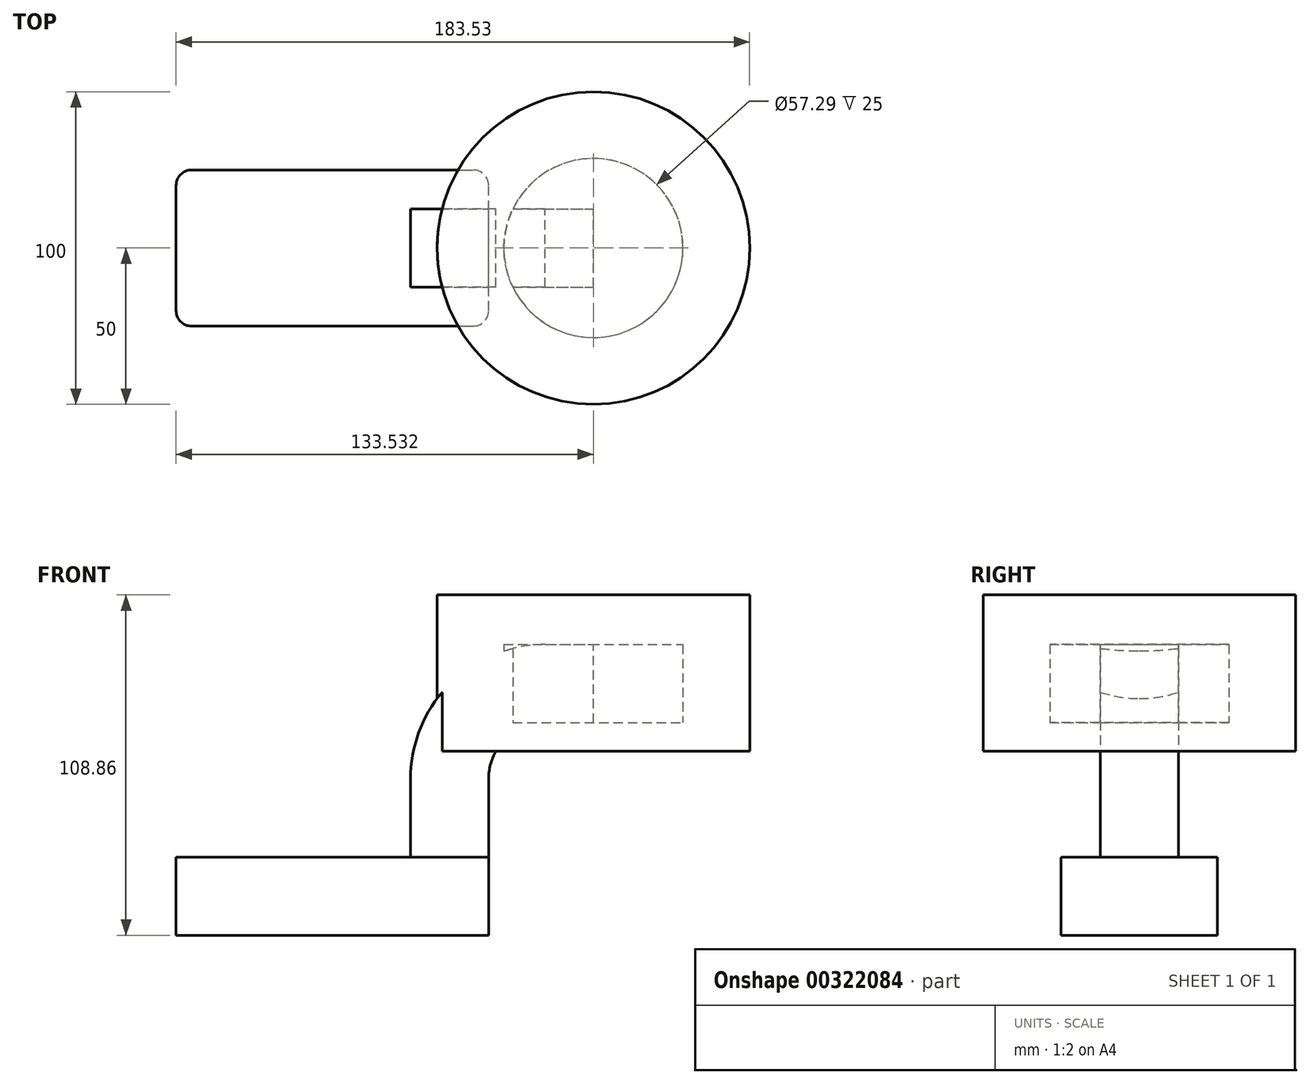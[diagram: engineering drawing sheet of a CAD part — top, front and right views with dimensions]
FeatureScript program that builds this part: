
annotation { "Feature Type Name" : "Feature", "Feature Type Description" : "" }
export const myFeature = defineFeature(function(context is Context, id is Id, definition is map)
    precondition{}
    {
        {
            var Q0;
            Q0=qCreatedBy(makeId("Front.planeOp"),FACE);
            var sketch = newSketch(context, id + "F0", { "sketchPlane" : qUnion([Q0])});
            skLineSegment(sketch, "E0.bottom", {"start": v(-50, 12.5) * mm, "end": v(50, 12.5) * mm});
            skLineSegment(sketch, "E0.top", {"start": v(-50, -12.5) * mm, "end": v(50, -12.5) * mm});
            skLineSegment(sketch, "E0.left", {"start": v(-50, 12.5) * mm, "end": v(-50, -12.5) * mm});
            skLineSegment(sketch, "E0.right", {"start": v(50, 12.5) * mm, "end": v(50, -12.5) * mm});
            skPoint(sketch, "E0.middle", {"position": v(0, 0) * mm});
            skLineSegment(sketch, "E1.bottom", {"start": v(133.53, 46.36) * mm, "end": v(83.53, 46.36) * mm});
            skLineSegment(sketch, "E1.top", {"start": v(133.53, 96.36) * mm, "end": v(83.53, 96.36) * mm});
            skLineSegment(sketch, "E1.left", {"start": v(133.53, 46.36) * mm, "end": v(133.53, 96.36) * mm});
            skLineSegment(sketch, "E1.right", {"start": v(83.53, 46.36) * mm, "end": v(83.53, 96.36) * mm});
            skPoint(sketch, "E1.middle", {"position": v(108.53, 71.36) * mm});
            skLineSegment(sketch, "E2", {"start": v(50, 12.5) * mm, "end": v(50, 37.5) * mm});
            skArc(sketch, "E3", {"start": v(50, 37.5) * mm, "mid": v(55.27, 50.23) * mm, "end": v(68, 55.5) * mm});
            skLineSegment(sketch, "E4", {"start": v(68, 55.5) * mm, "end": v(112.18, 55.5) * mm});
            skLineSegment(sketch, "E5.0", {"start": v(68, 80.5) * mm, "end": v(112.18, 80.5) * mm});
            skArc(sketch, "E5.1", {"start": v(25, 37.5) * mm, "mid": v(37.6, 67.9) * mm, "end": v(68, 80.5) * mm});
            skLineSegment(sketch, "E5.2", {"start": v(25, 12.5) * mm, "end": v(25, 37.5) * mm});
            skLineSegment(sketch, "E6", {"start": v(112.18, 55.5) * mm, "end": v(112.18, 80.5) * mm});
            skFitSpline(sketch, "E7", {"points": [v(-50, 12.5) * mm, v(68, 80.5) * mm], "startDerivative": vector(61.6, 119.2) * mm, "endDerivative": vector(204, -25) * mm});
            skSolve(sketch);
        }
        {
            var Q0;
            Q0=makeQuery(id+"F0.imprint","IMPRINT",FACE,{"disambiguationData":[TD([[makeQuery(id+"F0.imprint","IMPRINT",EDGE,{"derivedFrom":sQuery(id+"F0.wireOp",EDGE,"E0.top")}),1.0]])]});
            extrude(context, id + "F1", {"entities" : qUnion([Q0]), "endBound" : BoundingType.SYMMETRIC, "depth" : 50 * mm});
        }
        {
            var Q0;
            Q0=makeQuery(id+"F0.imprint","IMPRINT",FACE,{"disambiguationData":[TD([[makeQuery(id+"F0.imprint","IMPRINT",EDGE,{"derivedFrom":sQuery(id+"F0.wireOp",EDGE,"E5.1")}),1.0]])]});
            var Q1;
            {var subQ1=sQuery(id+"F0.wireOp",EDGE,"E2");Q1=makeQuery(id+"F0.imprint","IMPRINT",FACE,{"disambiguationData":[TD([[makeQuery(id+"F0.imprint","IMPRINT",EDGE,{"derivedFrom":subQ1}),1.0]])]});}
            extrude(context, id + "F2", {"entities" : qUnion([Q0, Q1]), "endBound" : BoundingType.SYMMETRIC, "depth" : 25 * mm});
        }
        {
            var Q0;
            {var subQ1=sQuery(id+"F0.wireOp",EDGE,"E1.bottom");Q0=makeQuery(id+"F0.imprint","IMPRINT",FACE,{"disambiguationData":[TD([[makeQuery(id+"F0.imprint","IMPRINT",EDGE,{"derivedFrom":subQ1}),-1.0]])]});}
            var Q1;
            Q1=sQuery(id+"F0.wireOp",EDGE,"E1.right");
            revolve(context, id + "F3", {"operationType" : NewBodyOperationType.ADD, "entities" : qUnion([Q0]), "axis" : qUnion([Q1]), "revolveType" : RevolveType.FULL});
        }
        {
            var Q0;
            Q0=makeQuery(id+"F1.opExtrude","CAP_EDGE",EDGE,{"disambiguationData":[OSD([sQuery(id+"F0.wireOp",EDGE,"E0.left")])],"isStart":false});
            var Q1;
            Q1=makeQuery(id+"F1.opExtrude","CAP_EDGE",EDGE,{"disambiguationData":[OSD([sQuery(id+"F0.wireOp",EDGE,"E0.right")])],"isStart":false});
            var Q2;
            Q2=makeQuery(id+"F1.opExtrude","CAP_EDGE",EDGE,{"disambiguationData":[OSD([sQuery(id+"F0.wireOp",EDGE,"E0.right")])],"isStart":true});
            var Q3;
            Q3=makeQuery(id+"F1.opExtrude","CAP_EDGE",EDGE,{"disambiguationData":[OSD([sQuery(id+"F0.wireOp",EDGE,"E0.left")])],"isStart":true});
            fillet(context, id + "F4", {"entities" : qUnion([Q0, Q1, Q2, Q3]), "radius" : 5 * mm, "tangentPropagation" : true, "allowEdgeOverflow" : false});
        }
    });
